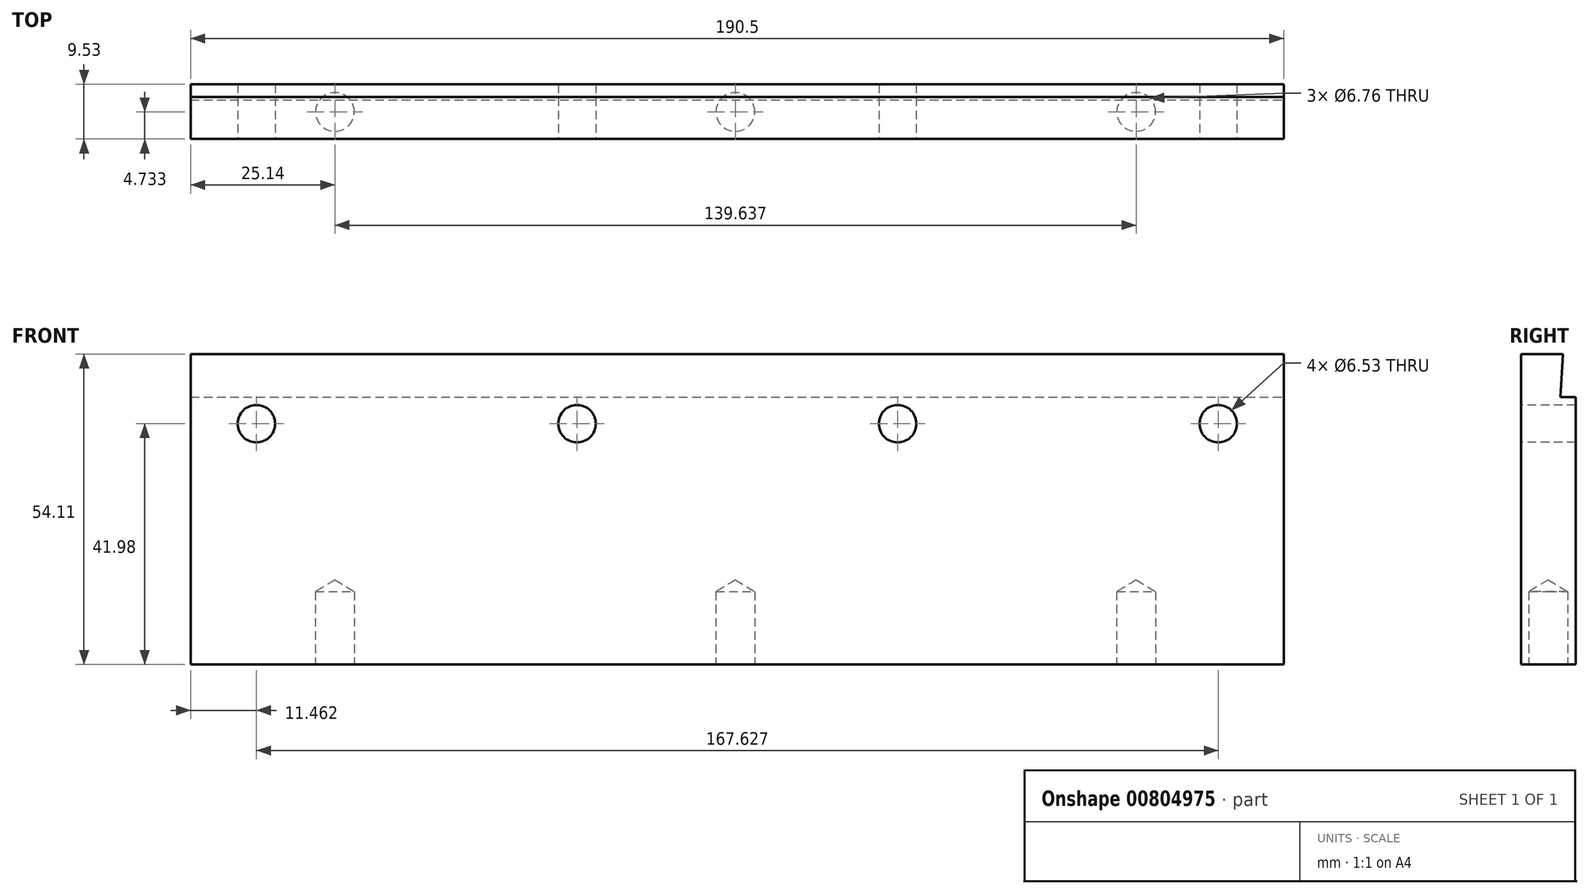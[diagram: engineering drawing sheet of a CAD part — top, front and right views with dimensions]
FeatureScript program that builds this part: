
annotation { "Feature Type Name" : "Feature", "Feature Type Description" : "" }
export const myFeature = defineFeature(function(context is Context, id is Id, definition is map)
    precondition{}
    {
        {
            var Q0;
            Q0=qCreatedBy(makeId("Front.planeOp"),FACE);
            var sketch = newSketch(context, id + "F0", { "sketchPlane" : qUnion([Q0])});
            skLineSegment(sketch, "E0.bottom", {"start": v(0, 0) * mm, "end": v(190.5, 0) * mm});
            skLineSegment(sketch, "E0.top", {"start": v(0, 54.11) * mm, "end": v(190.5, 54.11) * mm});
            skLineSegment(sketch, "E0.left", {"start": v(0, 0) * mm, "end": v(0, 54.11) * mm});
            skLineSegment(sketch, "E0.right", {"start": v(190.5, 0) * mm, "end": v(190.5, 54.11) * mm});
            skSolve(sketch);
        }
        {
            var Q0;
            Q0 = qSketchRegion(id + "F0", true);
            extrude(context, id + "F1", {"entities" : qUnion([Q0]), "depth" : 9.52 * mm, "offsetDistance" : 25.4 * mm});
        }
        {
            var Q0;
            Q0=makeQuery(id+"F1.opExtrude","CAP_FACE",FACE,{"disambiguationData":[OSD([sQuery(id+"F0.wireOp",EDGE,"E0.bottom"),sQuery(id+"F0.wireOp",EDGE,"E0.top"),sQuery(id+"F0.wireOp",EDGE,"E0.left"),sQuery(id+"F0.wireOp",EDGE,"E0.right")])],"isStart":false});
            var sketch = newSketch(context, id + "F2", { "sketchPlane" : qUnion([Q0])});
            skCircle(sketch, "E1", {"center": v(11.46, 41.98) * mm, "radius": 3.36 * mm, "construction": true});
            skCircle(sketch, "E2", {"center": v(67.34, 41.98) * mm, "radius": 3.36 * mm, "construction": true});
            skCircle(sketch, "E3", {"center": v(123.2, 41.98) * mm, "radius": 3.36 * mm, "construction": true});
            skCircle(sketch, "E4", {"center": v(179.09, 41.98) * mm, "radius": 3.36 * mm, "construction": true});
            skSolve(sketch);
        }
        {
            var Q0;
            Q0=sQuery(id+"F2.wireOp",VERTEX,"E1.center");
            var Q1;
            Q1=sQuery(id+"F2.wireOp",VERTEX,"E2.center");
            var Q2;
            Q2=sQuery(id+"F2.wireOp",VERTEX,"E3.center");
            var Q3;
            Q3=sQuery(id+"F2.wireOp",VERTEX,"E4.center");
            var Q4;
            Q4=makeQuery(id+"F1.opExtrude","SWEPT_BODY",BODY,{"disambiguationData":[OSD([sQuery(id+"F0.wireOp",EDGE,"E0.bottom"),sQuery(id+"F0.wireOp",EDGE,"E0.top"),sQuery(id+"F0.wireOp",EDGE,"E0.left"),sQuery(id+"F0.wireOp",EDGE,"E0.right")])]});
            hole(context, id + "F3", {"style" : HoleStyle.SIMPLE, "endStyle" : HoleEndStyle.THROUGH, "standardTappedOrClearance" : lookupTablePath({ "standard" : "ANSI", "engagement" : "75%", "pitch" : "18 tpi", "size" : "5/16", "type" : "Tapped" }), "standardBlindInLast" : lookupTablePath({ "standard" : "ANSI", "fit" : "Free", "engagement" : "75%", "pitch" : "18 tpi", "size" : "5/16", "type" : "Clearance & tapped" }), "holeDiameter" : 6.53 * mm, "majorDiameter" : 7.94 * mm, "showTappedDepth" : true, "isTappedThrough" : true, "tappedDepth" : 21.17 * mm, "tapClearance" : 3, "startFromSketch" : true, "locations" : qUnion([Q0, Q1, Q2, Q3]), "scope" : qUnion([Q4])});
        }
        {
            var Q0;
            Q0=makeQuery(id+"F1.opExtrude","SWEPT_FACE",FACE,{"disambiguationData":[OSD([sQuery(id+"F0.wireOp",EDGE,"E0.right")])]});
            var sketch = newSketch(context, id + "F4", { "sketchPlane" : qUnion([Q0])});
            skLineSegment(sketch, "E5", {"start": v(-2.2, 54.11) * mm, "end": v(-2.7, 46.63) * mm});
            skLineSegment(sketch, "E6", {"start": v(-2.7, 46.63) * mm, "end": v(0, 46.63) * mm});
            skLineSegment(sketch, "E7", {"start": v(0, 46.63) * mm, "end": v(0, 54.11) * mm});
            skLineSegment(sketch, "E8", {"start": v(0, 54.11) * mm, "end": v(-2.2, 54.11) * mm});
            skSolve(sketch);
        }
        {
            var Q0;
            Q0 = qSketchRegion(id + "F4", true);
            extrude(context, id + "F5", {"entities" : qUnion([Q0]), "operationType" : NewBodyOperationType.REMOVE, "endBound" : BoundingType.THROUGH_ALL, "oppositeDirection" : true, "depth" : 25.4 * mm, "offsetDistance" : 25.4 * mm});
        }
        {
            var Q0;
            Q0=makeQuery(id+"F1.opExtrude","SWEPT_FACE",FACE,{"disambiguationData":[OSD([sQuery(id+"F0.wireOp",EDGE,"E0.bottom")])]});
            var sketch = newSketch(context, id + "F6", { "sketchPlane" : qUnion([Q0])});
            skCircle(sketch, "E9", {"center": v(25.14, 4.8) * mm, "radius": 3.35 * mm, "construction": true});
            skCircle(sketch, "E10", {"center": v(94.93, 4.8) * mm, "radius": 3.35 * mm, "construction": true});
            skCircle(sketch, "E11", {"center": v(164.78, 4.8) * mm, "radius": 3.35 * mm, "construction": true});
            skSolve(sketch);
        }
        {
            var Q0;
            Q0=sQuery(id+"F6.wireOp",VERTEX,"E9.center");
            var Q1;
            Q1=sQuery(id+"F6.wireOp",VERTEX,"E10.center");
            var Q2;
            Q2=sQuery(id+"F6.wireOp",VERTEX,"E11.center");
            var Q3;
            Q3=makeQuery(id+"F1.opExtrude","SWEPT_BODY",BODY,{"disambiguationData":[OSD([sQuery(id+"F0.wireOp",EDGE,"E0.bottom"),sQuery(id+"F0.wireOp",EDGE,"E0.top"),sQuery(id+"F0.wireOp",EDGE,"E0.left"),sQuery(id+"F0.wireOp",EDGE,"E0.right")])]});
            hole(context, id + "F7", {"style" : HoleStyle.SIMPLE, "endStyle" : HoleEndStyle.BLIND, "standardTappedOrClearance" : lookupTablePath({ "fit" : "Free", "standard" : "ANSI", "size" : "1/4", "type" : "Clearance" }), "standardBlindInLast" : lookupTablePath({ "fit" : "Free", "standard" : "ANSI", "engagement" : "75%", "pitch" : "20 tpi", "size" : "1/4", "type" : "Clearance & tapped" }), "holeDiameter" : 6.76 * mm, "majorDiameter" : 6.35 * mm, "holeDepth" : 12.7 * mm, "isTappedThrough" : true, "tappedDepth" : 21.17 * mm, "tapClearance" : 3, "startFromSketch" : true, "locations" : qUnion([Q0, Q1, Q2]), "scope" : qUnion([Q3])});
        }
    });
